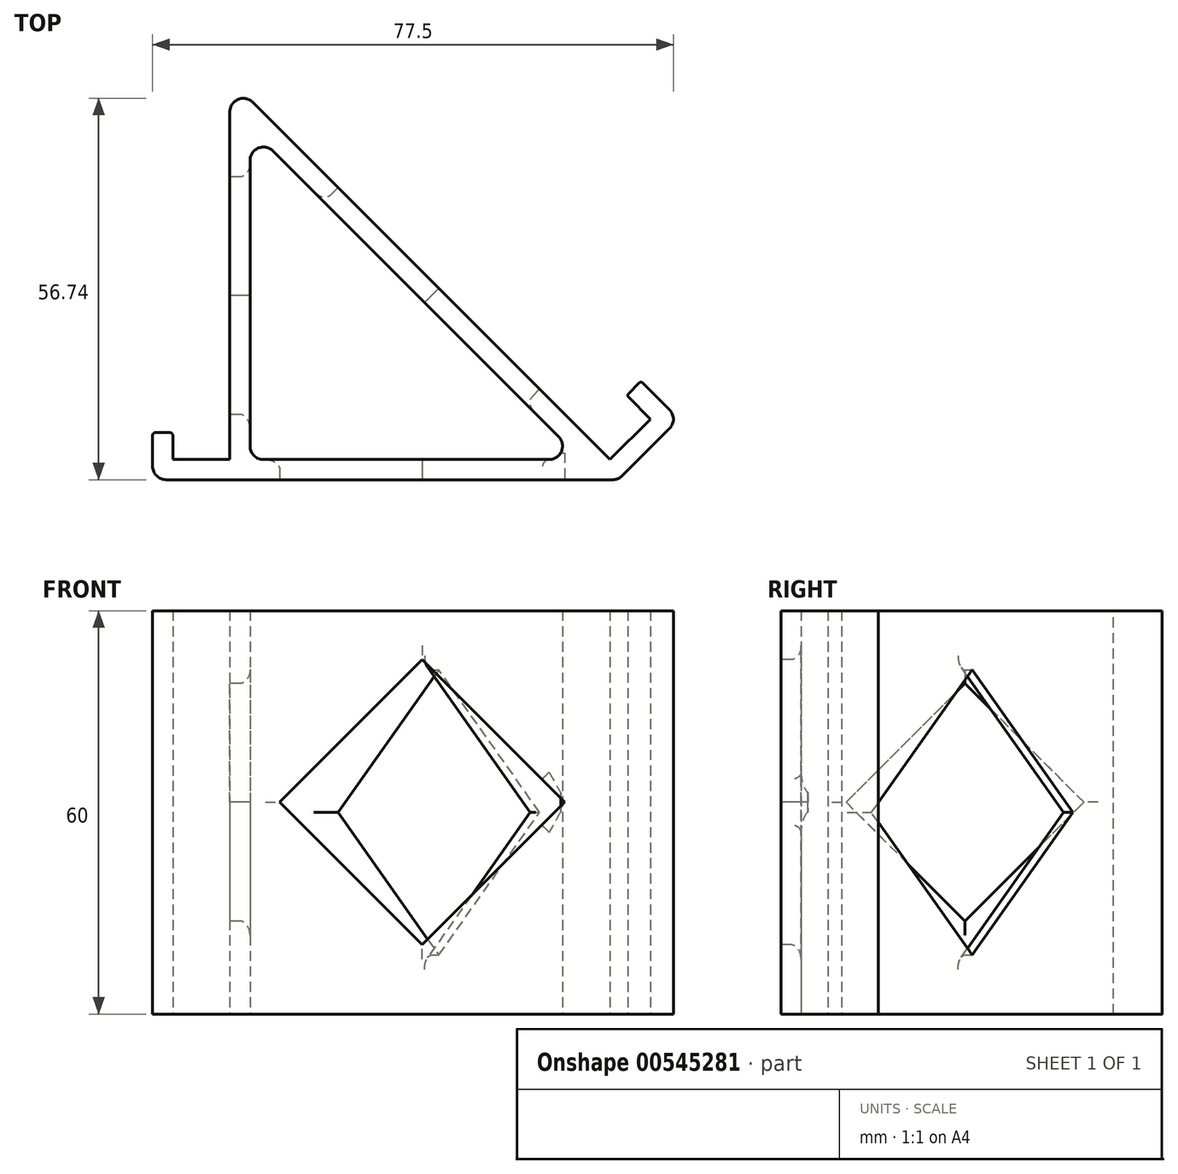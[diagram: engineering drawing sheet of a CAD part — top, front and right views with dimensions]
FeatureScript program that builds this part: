
annotation { "Feature Type Name" : "Feature", "Feature Type Description" : "" }
export const myFeature = defineFeature(function(context is Context, id is Id, definition is map)
    precondition{}
    {
        {
            var Q0;
            Q0=qCreatedBy(makeId("Top.planeOp"),FACE);
            var sketch = newSketch(context, id + "F0", { "sketchPlane" : qUnion([Q0])});
            skLineSegment(sketch, "E0.bottom", {"start": v(27.73, -27.47) * mm, "end": v(-41.59, -27.47) * mm});
            skLineSegment(sketch, "E0.top", {"start": v(22.24, -24.47) * mm, "end": v(-27.09, -24.47) * mm});
            skLineSegment(sketch, "E1", {"start": v(27.73, -27.47) * mm, "end": v(36.74, -18.46) * mm});
            skLineSegment(sketch, "E2", {"start": v(36.74, -18.46) * mm, "end": v(31.08, -12.8) * mm});
            skLineSegment(sketch, "E3", {"start": v(31.08, -12.8) * mm, "end": v(28.96, -14.92) * mm});
            skLineSegment(sketch, "E4", {"start": v(28.96, -14.92) * mm, "end": v(32.5, -18.46) * mm});
            skLineSegment(sketch, "E5", {"start": v(32.5, -18.46) * mm, "end": v(26.48, -24.47) * mm});
            skLineSegment(sketch, "E6", {"start": v(26.48, -24.47) * mm, "end": v(-30.09, 32.1) * mm});
            skLineSegment(sketch, "E7", {"start": v(22.24, -24.47) * mm, "end": v(-27.09, 24.86) * mm});
            skLineSegment(sketch, "E8", {"start": v(-30.09, 32.1) * mm, "end": v(-30.09, -24.47) * mm});
            skLineSegment(sketch, "E9", {"start": v(-27.09, 24.86) * mm, "end": v(-27.09, -24.47) * mm});
            skLineSegment(sketch, "E10", {"start": v(-30.09, -24.47) * mm, "end": v(-38.59, -24.47) * mm});
            skLineSegment(sketch, "E11", {"start": v(-41.59, -27.47) * mm, "end": v(-41.59, -24.47) * mm});
            skLineSegment(sketch, "E12", {"start": v(-41.59, -24.47) * mm, "end": v(-41.59, -20.47) * mm});
            skLineSegment(sketch, "E13", {"start": v(-41.59, -20.47) * mm, "end": v(-38.59, -20.47) * mm});
            skLineSegment(sketch, "E14", {"start": v(-38.59, -20.47) * mm, "end": v(-38.59, -24.47) * mm});
            skSolve(sketch);
        }
        {
            var Q0;
            Q0 = qSketchRegion(id + "F0", true);
            extrude(context, id + "F1", {"entities" : qUnion([Q0]), "depth" : 60 * mm, "offsetDistance" : 25 * mm});
        }
        {
            var Q0;
            Q0=makeQuery(id+"F1.opExtrude","SWEPT_EDGE",EDGE,{"disambiguationData":[OSD([sQuery(id+"F0.wireOp",EDGE,"E6"),sQuery(id+"F0.wireOp",EDGE,"E8")])]});
            var Q1;
            Q1=makeQuery(id+"F1.opExtrude","SWEPT_EDGE",EDGE,{"disambiguationData":[OSD([sQuery(id+"F0.wireOp",EDGE,"E1"),sQuery(id+"F0.wireOp",EDGE,"E2")])]});
            var Q2;
            Q2=makeQuery(id+"F1.opExtrude","SWEPT_EDGE",EDGE,{"disambiguationData":[OSD([sQuery(id+"F0.wireOp",EDGE,"E0.bottom"),sQuery(id+"F0.wireOp",EDGE,"E1")])]});
            var Q3;
            Q3=makeQuery(id+"F1.opExtrude","SWEPT_EDGE",EDGE,{"disambiguationData":[OSD([sQuery(id+"F0.wireOp",EDGE,"E0.bottom"),sQuery(id+"F0.wireOp",EDGE,"E11")])]});
            var Q4;
            Q4=makeQuery(id+"F1.opExtrude","SWEPT_EDGE",EDGE,{"disambiguationData":[OSD([sQuery(id+"F0.wireOp",EDGE,"E0.top"),sQuery(id+"F0.wireOp",EDGE,"E9")])]});
            var Q5;
            Q5=makeQuery(id+"F1.opExtrude","SWEPT_EDGE",EDGE,{"disambiguationData":[OSD([sQuery(id+"F0.wireOp",EDGE,"E0.top"),sQuery(id+"F0.wireOp",EDGE,"E7")])]});
            var Q6;
            Q6=makeQuery(id+"F1.opExtrude","SWEPT_EDGE",EDGE,{"disambiguationData":[OSD([sQuery(id+"F0.wireOp",EDGE,"E7"),sQuery(id+"F0.wireOp",EDGE,"E9")])]});
            fillet(context, id + "F2", {"entities" : qUnion([Q0, Q1, Q2, Q3, Q4, Q5, Q6]), "radius" : 2 * mm, "tangentPropagation" : true, "allowEdgeOverflow" : false});
        }
        {
            var Q0;
            Q0=makeQuery(id+"F1.opExtrude","SWEPT_FACE",FACE,{"disambiguationData":[OSD([sQuery(id+"F0.wireOp",EDGE,"E6")])]});
            cPlane(context, id + "F3", {"entities" : qUnion([Q0]), "cplaneType" : CPlaneType.OFFSET, "offset" : 0 * mm, "width" : 150 * mm, "height" : 150 * mm});
        }
        {
            var Q0;
            Q0=qCreatedBy(id+"F3.planeOp",FACE);
            var sketch = newSketch(context, id + "F4", { "sketchPlane" : qUnion([Q0])});
            skCircle(sketch, "E15.cCircle", {"center": v(0, 30) * mm, "radius": 15 * mm, "construction": true});
            skLineSegment(sketch, "E15.0", {"start": v(0, 8.79) * mm, "end": v(-21.21, 30) * mm});
            skLineSegment(sketch, "E15.1", {"start": v(-21.21, 30) * mm, "end": v(0, 51.21) * mm});
            skLineSegment(sketch, "E15.2", {"start": v(0, 51.21) * mm, "end": v(21.21, 30) * mm});
            skLineSegment(sketch, "E15.3", {"start": v(21.21, 30) * mm, "end": v(0, 8.79) * mm});
            skPoint(sketch, "E15.0.midPoint", {"position": v(-10.6, 19.4) * mm});
            skLineSegment(sketch, "E16", {"start": v(0, 30) * mm, "end": v(21.21, 30) * mm});
            skSolve(sketch);
        }
        {
            var Q0;
            Q0 = qSketchRegion(id + "F4", true);
            extrude(context, id + "F5", {"entities" : qUnion([Q0]), "operationType" : NewBodyOperationType.REMOVE, "oppositeDirection" : true, "depth" : 4 * mm, "offsetDistance" : 25 * mm});
        }
        {
            var Q0;
            Q0=makeQuery(id+"F1.opExtrude","SWEPT_FACE",FACE,{"disambiguationData":[OSD([sQuery(id+"F0.wireOp",EDGE,"E8")])]});
            var sketch = newSketch(context, id + "F6", { "sketchPlane" : qUnion([Q0])});
            skCircle(sketch, "E17.cCircle", {"center": v(0.07, 31.52) * mm, "radius": 12.5 * mm, "construction": true});
            skLineSegment(sketch, "E17.0", {"start": v(0.07, 13.84) * mm, "end": v(-17.6, 31.52) * mm});
            skLineSegment(sketch, "E17.1", {"start": v(-17.6, 31.52) * mm, "end": v(0.07, 49.2) * mm});
            skLineSegment(sketch, "E17.2", {"start": v(0.07, 49.2) * mm, "end": v(17.75, 31.52) * mm});
            skLineSegment(sketch, "E17.3", {"start": v(17.75, 31.52) * mm, "end": v(0.07, 13.84) * mm});
            skPoint(sketch, "E17.0.midPoint", {"position": v(-8.76, 22.68) * mm});
            skLineSegment(sketch, "E18", {"start": v(0.07, 31.52) * mm, "end": v(17.75, 31.52) * mm});
            skSolve(sketch);
        }
        {
            var Q0;
            Q0 = qSketchRegion(id + "F6", true);
            extrude(context, id + "F7", {"entities" : qUnion([Q0]), "operationType" : NewBodyOperationType.REMOVE, "oppositeDirection" : true, "depth" : 4 * mm, "offsetDistance" : 25 * mm});
        }
        {
            var Q0;
            Q0=makeQuery(id+"F1.opExtrude","SWEPT_FACE",FACE,{"disambiguationData":[OSD([sQuery(id+"F0.wireOp",EDGE,"E0.bottom")])]});
            var sketch = newSketch(context, id + "F8", { "sketchPlane" : qUnion([Q0])});
            skCircle(sketch, "E19.cCircle", {"center": v(-1.45, 31.52) * mm, "radius": 15 * mm, "construction": true});
            skLineSegment(sketch, "E19.0", {"start": v(-1.45, 10.3) * mm, "end": v(-22.67, 31.52) * mm});
            skLineSegment(sketch, "E19.1", {"start": v(-22.67, 31.52) * mm, "end": v(-1.45, 52.73) * mm});
            skLineSegment(sketch, "E19.2", {"start": v(-1.45, 52.73) * mm, "end": v(19.76, 31.52) * mm});
            skLineSegment(sketch, "E19.3", {"start": v(19.76, 31.52) * mm, "end": v(-1.45, 10.3) * mm});
            skPoint(sketch, "E19.0.midPoint", {"position": v(-12.06, 20.9) * mm});
            skLineSegment(sketch, "E20", {"start": v(-1.45, 31.52) * mm, "end": v(19.76, 31.52) * mm});
            skSolve(sketch);
        }
        {
            var Q0;
            Q0 = qSketchRegion(id + "F8", true);
            extrude(context, id + "F9", {"entities" : qUnion([Q0]), "operationType" : NewBodyOperationType.REMOVE, "oppositeDirection" : true, "depth" : 4 * mm, "offsetDistance" : 25 * mm});
        }
        {
            var Q0;
            Q0=makeQuery(id+"F1.opExtrude","SWEPT_EDGE",EDGE,{"disambiguationData":[OSD([sQuery(id+"F0.wireOp",EDGE,"E3"),sQuery(id+"F0.wireOp",EDGE,"E4")])]});
            var Q1;
            Q1=makeQuery(id+"F1.opExtrude","SWEPT_EDGE",EDGE,{"disambiguationData":[OSD([sQuery(id+"F0.wireOp",EDGE,"E2"),sQuery(id+"F0.wireOp",EDGE,"E3")])]});
            var Q2;
            Q2=makeQuery(id+"F1.opExtrude","SWEPT_EDGE",EDGE,{"disambiguationData":[OSD([sQuery(id+"F0.wireOp",EDGE,"E12"),sQuery(id+"F0.wireOp",EDGE,"E13")])]});
            var Q3;
            Q3=makeQuery(id+"F1.opExtrude","SWEPT_EDGE",EDGE,{"disambiguationData":[OSD([sQuery(id+"F0.wireOp",EDGE,"E13"),sQuery(id+"F0.wireOp",EDGE,"E14")])]});
            fillet(context, id + "F10", {"entities" : qUnion([Q0, Q1, Q2, Q3]), "radius" : 0.4 * mm, "tangentPropagation" : true, "allowEdgeOverflow" : false});
        }
        {
            var Q0;
            Q0=makeQuery(id+"F7.boolean.opBoolean","COPY",EDGE,{"derivedFrom":makeQuery(id+"F7.opExtrude","CAP_EDGE",EDGE,{"disambiguationData":[OSD([sQuery(id+"F6.wireOp",EDGE,"E17.3")])],"isStart":true})});
            var Q1;
            Q1=makeQuery(id+"F7.boolean.opBoolean","INTERSECT",EDGE,{"derivedFrom":[makeQuery(id+"F1.opExtrude","SWEPT_FACE",FACE,{"disambiguationData":[OSD([sQuery(id+"F0.wireOp",EDGE,"E9")])]}),makeQuery(id+"F7.opExtrude","SWEPT_FACE",FACE,{"disambiguationData":[OSD([sQuery(id+"F6.wireOp",EDGE,"E17.3")])]})]});
            var Q2;
            Q2=makeQuery(id+"F7.boolean.opBoolean","COPY",EDGE,{"derivedFrom":makeQuery(id+"F7.opExtrude","CAP_EDGE",EDGE,{"disambiguationData":[OSD([sQuery(id+"F6.wireOp",EDGE,"E17.2")])],"isStart":true})});
            var Q3;
            Q3=makeQuery(id+"F7.boolean.opBoolean","INTERSECT",EDGE,{"derivedFrom":[makeQuery(id+"F1.opExtrude","SWEPT_FACE",FACE,{"disambiguationData":[OSD([sQuery(id+"F0.wireOp",EDGE,"E9")])]}),makeQuery(id+"F7.opExtrude","SWEPT_FACE",FACE,{"disambiguationData":[OSD([sQuery(id+"F6.wireOp",EDGE,"E17.2")])]})]});
            var Q4;
            Q4=makeQuery(id+"F7.boolean.opBoolean","COPY",EDGE,{"derivedFrom":makeQuery(id+"F7.opExtrude","CAP_EDGE",EDGE,{"disambiguationData":[OSD([sQuery(id+"F6.wireOp",EDGE,"E17.1")])],"isStart":true})});
            var Q5;
            Q5=makeQuery(id+"F7.boolean.opBoolean","COPY",EDGE,{"derivedFrom":makeQuery(id+"F7.opExtrude","CAP_EDGE",EDGE,{"disambiguationData":[OSD([sQuery(id+"F6.wireOp",EDGE,"E17.0")])],"isStart":true})});
            var Q6;
            Q6=makeQuery(id+"F7.boolean.opBoolean","INTERSECT",EDGE,{"derivedFrom":[makeQuery(id+"F1.opExtrude","SWEPT_FACE",FACE,{"disambiguationData":[OSD([sQuery(id+"F0.wireOp",EDGE,"E9")])]}),makeQuery(id+"F7.opExtrude","SWEPT_FACE",FACE,{"disambiguationData":[OSD([sQuery(id+"F6.wireOp",EDGE,"E17.1")])]})]});
            var Q7;
            Q7=makeQuery(id+"F7.boolean.opBoolean","INTERSECT",EDGE,{"derivedFrom":[makeQuery(id+"F1.opExtrude","SWEPT_FACE",FACE,{"disambiguationData":[OSD([sQuery(id+"F0.wireOp",EDGE,"E9")])]}),makeQuery(id+"F7.opExtrude","SWEPT_FACE",FACE,{"disambiguationData":[OSD([sQuery(id+"F6.wireOp",EDGE,"E17.0")])]})]});
            fillet(context, id + "F11", {"entities" : qUnion([Q0, Q1, Q2, Q3, Q4, Q5, Q6, Q7]), "radius" : 1.5 * mm, "tangentPropagation" : true, "allowEdgeOverflow" : false});
        }
        {
            var Q0;
            Q0=makeQuery(id+"F5.boolean.opBoolean","COPY",EDGE,{"derivedFrom":makeQuery(id+"F5.opExtrude","CAP_EDGE",EDGE,{"disambiguationData":[OSD([sQuery(id+"F4.wireOp",EDGE,"E15.3")])],"isStart":true})});
            var Q1;
            Q1=makeQuery(id+"F5.boolean.opBoolean","COPY",EDGE,{"derivedFrom":makeQuery(id+"F5.opExtrude","CAP_EDGE",EDGE,{"disambiguationData":[OSD([sQuery(id+"F4.wireOp",EDGE,"E15.2")])],"isStart":true})});
            var Q2;
            Q2=makeQuery(id+"F5.boolean.opBoolean","COPY",EDGE,{"derivedFrom":makeQuery(id+"F5.opExtrude","CAP_EDGE",EDGE,{"disambiguationData":[OSD([sQuery(id+"F4.wireOp",EDGE,"E15.1")])],"isStart":true})});
            var Q3;
            Q3=makeQuery(id+"F5.boolean.opBoolean","COPY",EDGE,{"derivedFrom":makeQuery(id+"F5.opExtrude","CAP_EDGE",EDGE,{"disambiguationData":[OSD([sQuery(id+"F4.wireOp",EDGE,"E15.0")])],"isStart":true})});
            var Q4;
            Q4=makeQuery(id+"F5.boolean.opBoolean","INTERSECT",EDGE,{"derivedFrom":[makeQuery(id+"F1.opExtrude","SWEPT_FACE",FACE,{"disambiguationData":[OSD([sQuery(id+"F0.wireOp",EDGE,"E7")])]}),makeQuery(id+"F5.opExtrude","SWEPT_FACE",FACE,{"disambiguationData":[OSD([sQuery(id+"F4.wireOp",EDGE,"E15.0")])]})]});
            var Q5;
            Q5=makeQuery(id+"F5.boolean.opBoolean","INTERSECT",EDGE,{"derivedFrom":[makeQuery(id+"F1.opExtrude","SWEPT_FACE",FACE,{"disambiguationData":[OSD([sQuery(id+"F0.wireOp",EDGE,"E7")])]}),makeQuery(id+"F5.opExtrude","SWEPT_FACE",FACE,{"disambiguationData":[OSD([sQuery(id+"F4.wireOp",EDGE,"E15.3")])]})]});
            var Q6;
            Q6=makeQuery(id+"F5.boolean.opBoolean","INTERSECT",EDGE,{"derivedFrom":[makeQuery(id+"F1.opExtrude","SWEPT_FACE",FACE,{"disambiguationData":[OSD([sQuery(id+"F0.wireOp",EDGE,"E7")])]}),makeQuery(id+"F5.opExtrude","SWEPT_FACE",FACE,{"disambiguationData":[OSD([sQuery(id+"F4.wireOp",EDGE,"E15.2")])]})]});
            var Q7;
            Q7=makeQuery(id+"F5.boolean.opBoolean","INTERSECT",EDGE,{"derivedFrom":[makeQuery(id+"F1.opExtrude","SWEPT_FACE",FACE,{"disambiguationData":[OSD([sQuery(id+"F0.wireOp",EDGE,"E7")])]}),makeQuery(id+"F5.opExtrude","SWEPT_FACE",FACE,{"disambiguationData":[OSD([sQuery(id+"F4.wireOp",EDGE,"E15.1")])]})]});
            var Q8;
            Q8=makeQuery(id+"F9.boolean.opBoolean","COPY",EDGE,{"derivedFrom":makeQuery(id+"F9.opExtrude","CAP_EDGE",EDGE,{"disambiguationData":[OSD([sQuery(id+"F8.wireOp",EDGE,"E19.1")])],"isStart":true})});
            var Q9;
            Q9=makeQuery(id+"F9.boolean.opBoolean","COPY",EDGE,{"derivedFrom":makeQuery(id+"F9.opExtrude","CAP_EDGE",EDGE,{"disambiguationData":[OSD([sQuery(id+"F8.wireOp",EDGE,"E19.2")])],"isStart":true})});
            var Q10;
            Q10=makeQuery(id+"F9.boolean.opBoolean","INTERSECT",EDGE,{"derivedFrom":[makeQuery(id+"F1.opExtrude","SWEPT_FACE",FACE,{"disambiguationData":[OSD([sQuery(id+"F0.wireOp",EDGE,"E0.top")])]}),makeQuery(id+"F9.opExtrude","SWEPT_FACE",FACE,{"disambiguationData":[OSD([sQuery(id+"F8.wireOp",EDGE,"E19.1")])]})]});
            var Q11;
            Q11=makeQuery(id+"F9.boolean.opBoolean","INTERSECT",EDGE,{"derivedFrom":[makeQuery(id+"F1.opExtrude","SWEPT_FACE",FACE,{"disambiguationData":[OSD([sQuery(id+"F0.wireOp",EDGE,"E0.top")])]}),makeQuery(id+"F9.opExtrude","SWEPT_FACE",FACE,{"disambiguationData":[OSD([sQuery(id+"F8.wireOp",EDGE,"E19.2")])]})]});
            var Q12;
            Q12=makeQuery(id+"F9.boolean.opBoolean","INTERSECT",EDGE,{"derivedFrom":[makeQuery(id+"F1.opExtrude","SWEPT_FACE",FACE,{"disambiguationData":[OSD([sQuery(id+"F0.wireOp",EDGE,"E0.top")])]}),makeQuery(id+"F9.opExtrude","SWEPT_FACE",FACE,{"disambiguationData":[OSD([sQuery(id+"F8.wireOp",EDGE,"E19.0")])]})]});
            var Q13;
            Q13=makeQuery(id+"F9.boolean.opBoolean","COPY",EDGE,{"derivedFrom":makeQuery(id+"F9.opExtrude","CAP_EDGE",EDGE,{"disambiguationData":[OSD([sQuery(id+"F8.wireOp",EDGE,"E19.0")])],"isStart":true})});
            var Q14;
            Q14=makeQuery(id+"F9.boolean.opBoolean","INTERSECT",EDGE,{"derivedFrom":[makeQuery(id+"F1.opExtrude","SWEPT_FACE",FACE,{"disambiguationData":[OSD([sQuery(id+"F0.wireOp",EDGE,"E0.top")])]}),makeQuery(id+"F9.opExtrude","SWEPT_FACE",FACE,{"disambiguationData":[OSD([sQuery(id+"F8.wireOp",EDGE,"E19.3")])]})]});
            var Q15;
            Q15=makeQuery(id+"F9.boolean.opBoolean","COPY",EDGE,{"derivedFrom":makeQuery(id+"F9.opExtrude","CAP_EDGE",EDGE,{"disambiguationData":[OSD([sQuery(id+"F8.wireOp",EDGE,"E19.3")])],"isStart":true})});
            fillet(context, id + "F12", {"entities" : qUnion([Q0, Q1, Q2, Q3, Q4, Q5, Q6, Q7, Q8, Q9, Q10, Q11, Q12, Q13, Q14, Q15]), "radius" : 1.5 * mm, "tangentPropagation" : true, "allowEdgeOverflow" : false});
        }
    });
